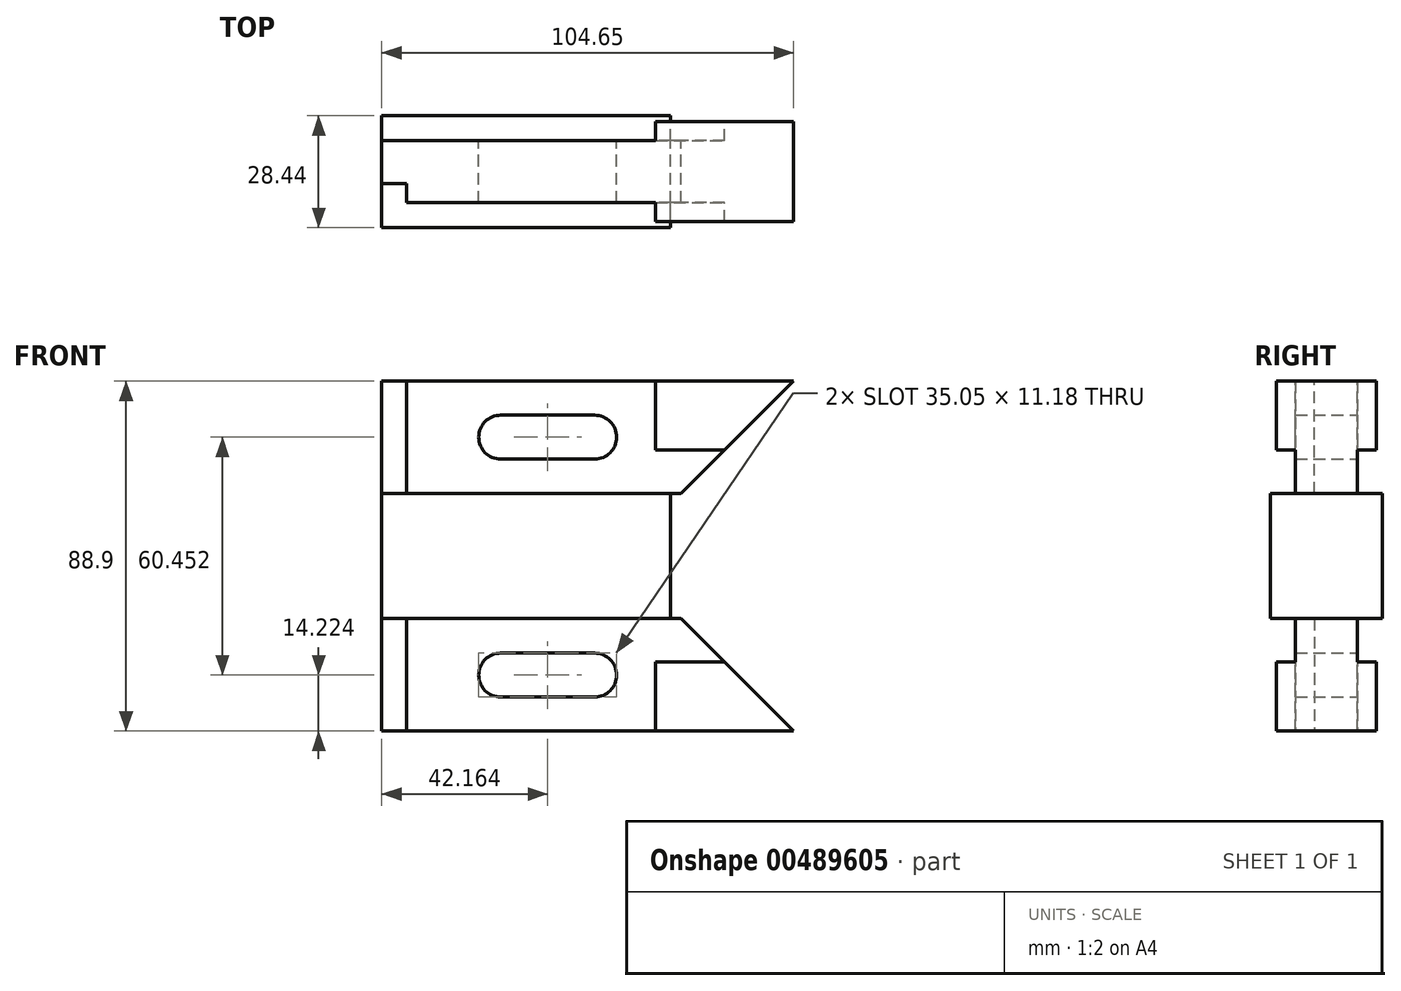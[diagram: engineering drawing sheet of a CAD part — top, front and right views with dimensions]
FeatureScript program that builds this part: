
annotation { "Feature Type Name" : "Feature", "Feature Type Description" : "" }
export const myFeature = defineFeature(function(context is Context, id is Id, definition is map)
    precondition{}
    {
        {
            var Q0;
            Q0=qCreatedBy(makeId("Front.planeOp"),FACE);
            var sketch = newSketch(context, id + "F0", { "sketchPlane" : qUnion([Q0])});
            skLineSegment(sketch, "E0.bottom", {"start": v(0, 0) * mm, "end": v(73.4, 0) * mm});
            skLineSegment(sketch, "E0.top", {"start": v(0, -15.88) * mm, "end": v(73.4, -15.88) * mm});
            skLineSegment(sketch, "E0.left", {"start": v(0, 0) * mm, "end": v(0, -15.88) * mm});
            skLineSegment(sketch, "E0.right", {"start": v(73.4, 0) * mm, "end": v(73.4, -15.88) * mm});
            skLineSegment(sketch, "E1", {"start": v(0, -15.88) * mm, "end": v(0, -44.45) * mm});
            skLineSegment(sketch, "E2", {"start": v(0, -44.45) * mm, "end": v(104.65, -44.45) * mm});
            skLineSegment(sketch, "E3", {"start": v(76.07, -15.88) * mm, "end": v(73.4, -15.88) * mm});
            skLineSegment(sketch, "E4", {"start": v(104.65, -44.45) * mm, "end": v(76.07, -15.87) * mm});
            skPoint(sketch, "E5.end.orphan", {"position": v(112.31, -15.88) * mm});
            skLineSegment(sketch, "E6", {"start": v(69.6, -44.45) * mm, "end": v(69.6, -26.92) * mm});
            skLineSegment(sketch, "E7", {"start": v(69.6, -26.92) * mm, "end": v(87.12, -26.92) * mm});
            skArc(sketch, "E8", {"start": v(30.23, -24.64) * mm, "mid": v(24.64, -30.23) * mm, "end": v(30.23, -35.81) * mm});
            skArc(sketch, "E9", {"start": v(54.1, -35.81) * mm, "mid": v(59.69, -30.23) * mm, "end": v(54.1, -24.64) * mm});
            skLineSegment(sketch, "E10", {"start": v(54.1, -24.64) * mm, "end": v(30.23, -24.64) * mm});
            skLineSegment(sketch, "E11", {"start": v(54.1, -35.81) * mm, "end": v(30.23, -35.81) * mm});
            skSolve(sketch);
        }
        {
            var Q0;
            Q0=makeQuery(id+"F0.imprint","IMPRINT",FACE,{"disambiguationData":[TD([[makeQuery(id+"F0.imprint","IMPRINT",EDGE,{"derivedFrom":sQuery(id+"F0.wireOp",EDGE,"E0.bottom")}),-1.0]])]});
            extrude(context, id + "F1", {"entities" : qUnion([Q0]), "endBound" : BoundingType.SYMMETRIC, "depth" : 28.45 * mm});
        }
        {
            var Q0;
            Q0=makeQuery(id+"F0.imprint","IMPRINT",FACE,{"disambiguationData":[TD([[makeQuery(id+"F0.imprint","IMPRINT",EDGE,{"derivedFrom":sQuery(id+"F0.wireOp",EDGE,"E0.top")}),-1.0]])]});
            extrude(context, id + "F2", {"entities" : qUnion([Q0]), "operationType" : NewBodyOperationType.ADD, "endBound" : BoundingType.SYMMETRIC, "depth" : 15.75 * mm});
        }
        {
            var Q0;
            {var subQ3=sQuery(id+"F0.wireOp",EDGE,"E6");Q0=makeQuery(id+"F0.imprint","IMPRINT",FACE,{"disambiguationData":[TD([[makeQuery(id+"F0.imprint","IMPRINT",EDGE,{"derivedFrom":subQ3}),-1.0]])]});}
            extrude(context, id + "F3", {"entities" : qUnion([Q0]), "operationType" : NewBodyOperationType.ADD, "endBound" : BoundingType.SYMMETRIC, "depth" : 25.4 * mm});
        }
        {
            var Q0;
            {var subQ0=sQuery(id+"F0.wireOp",EDGE,"E2");Q0=makeQuery(id+"F3.boolean.opBoolean","MERGE",FACE,{"derivedFrom":[makeQuery(id+"F2.opExtrude","SWEPT_FACE",FACE,{"disambiguationData":[OSD([subQ0])]}),makeQuery(id+"F3.opExtrude","SWEPT_FACE",FACE,{"disambiguationData":[OSD([subQ0])]})]});}
            var sketch = newSketch(context, id + "F4", { "sketchPlane" : qUnion([Q0])});
            skLineSegment(sketch, "E12", {"start": v(0, 3.05) * mm, "end": v(6.35, 3.05) * mm});
            skLineSegment(sketch, "E13", {"start": v(6.35, 3.05) * mm, "end": v(6.35, 7.87) * mm});
            skSolve(sketch);
        }
        {
            var Q0;
            {var subQ0=sQuery(id+"F4.wireOp",EDGE,"E12");Q0=makeQuery(id+"F4.imprint","IMPRINT",FACE,{"disambiguationData":[TD([[makeQuery(id+"F4.imprint","IMPRINT",EDGE,{"derivedFrom":subQ0}),1.0]])]});}
            var Q1;
            {var subQ0=sQuery(id+"F0.wireOp",EDGE,"E0.right");var subQ3=sQuery(id+"F0.wireOp",EDGE,"E0.top");var subQ4=sQuery(id+"F0.wireOp",EDGE,"E0.left");Q1=makeQuery(id+"F2.boolean.opBoolean","SPLIT",FACE,{"disambiguationData":[TD([makeQuery(id+"F1.opExtrude","CAP_FACE",FACE,{"disambiguationData":[OSD([sQuery(id+"F0.wireOp",EDGE,"E0.bottom"),subQ3,subQ4,subQ0])],"isStart":false})])],"derivedFrom":makeQuery(id+"F1.opExtrude","SWEPT_FACE",FACE,{"disambiguationData":[OSD([subQ3])]})});}
            extrude(context, id + "F5", {"entities" : qUnion([Q0]), "operationType" : NewBodyOperationType.REMOVE, "endBound" : BoundingType.UP_TO_SURFACE, "oppositeDirection" : true, "endBoundEntityFace" : qUnion([Q1]), "depth" : 25.4 * mm});
        }
        {
            var Q0;
            Q0=makeQuery(id+"F1.opExtrude","SWEPT_FACE",FACE,{"disambiguationData":[OSD([sQuery(id+"F0.wireOp",EDGE,"E0.bottom")])]});
            cPlane(context, id + "F6", {"entities" : qUnion([Q0]), "cplaneType" : CPlaneType.OFFSET, "offset" : 0 * mm, "width" : 152.4 * mm, "height" : 152.4 * mm});
        }
        {
            var Q0;
            Q0=makeQuery(id+"F1.opExtrude","SWEPT_BODY",BODY,{"disambiguationData":[OSD([sQuery(id+"F0.wireOp",EDGE,"E0.bottom"),sQuery(id+"F0.wireOp",EDGE,"E0.top"),sQuery(id+"F0.wireOp",EDGE,"E0.left"),sQuery(id+"F0.wireOp",EDGE,"E0.right")])]});
            var Q1;
            Q1=qCreatedBy(id+"F6.planeOp",FACE);
            mirror(context, id + "F7", {"operationType" : NewBodyOperationType.ADD, "entities" : qUnion([Q0]), "mirrorPlane" : qUnion([Q1])});
        }
    });
